# Revit family: 1195x595_START Panel Backlit UGR19
name_source: partatom
category: Lighting Fixtures
revit_build: Autodesk Revit 2017 (Build: 20190507_1515(x64)
units: mm (PartAtom-declared; Revit-internal decimal feet)

## family parameters
Cut with Voids When Loaded = No
Host = Face
Light Source = Yes
OmniClass Number = 23.80.70.00
OmniClass Title = Lighting
Part Type = Normal
Room Calculation Point = No
Round Connector Dimension = Use Diameter
Shared = No

## types (3) — shared parameters
-BOX_WIDTH_SYL = -40 mm
-LUMDEPTH_SYL = -277 mm
Apparent Load = 58 VA
Assembly Code = D5020200
AssetType = Fixed
BOX_WIDTH_SYL = 40 mm  [stored 0.131234 ft]
ClassificationName = Uniclass2015
ClassificationValue = EF_70_80
Color Filter = 16777215
DEPTH_SYL = 598 mm
Default Elevation = 1219 mm
Dimming Lamp Color Temperature Shift = <None>
DimmingControlOptions = http://www.sylvania-lighting.com
ElectricShockClassification = Class II
Emit Shape Visible in Rendering = No
Emit from Circle Diameter = 610 mm
HEIGHTBOTT_SYL = 7 mm  [stored 0.0229659 ft]
HEIGHT_SYL = 33 mm  [stored 0.108268 ft]
IfcExportAs = IfcLightFixtureType
IfcExportType = IfcLightFixtureType
ImpactProtectionIndex = IK03
IngressProtection = IP40/20
Keynote = 16500
LUMDEPTH_SYL = 277 mm
LUMWIDTH_SYL = 577 mm
Lamp = LED
LampColourRenderingIndex = 80
LampMacAdamStep = 6
LampsType = LED
LuminaireType = LED
MAINHEIGHT_SYL = 63 mm
Manufacturer = Feilo Sylvania
ManufacturerName = Feilo Sylvania
Material = aluminium,steel housing, other diffuser
Material_1_SYL = <By Category>
Material_2_SYL = <By Category>
Material_3_SYL = <By Category>
Material_4_SYL = <By Category>
NominalDepth = 595 mm  [stored 1.9521 ft]
NominalHeight = 35 mm
NominalLength = 1195 mm  [stored 3.9206 ft]
PowerConsumption = 58 W
PowerFactor = 0.9
TOP_DEPTH_SYL = 95 mm
TOP_WIDTH_SYL = 265 mm  [stored 0.869423 ft]
TOP__WIDTH_SYL = 545 mm
Tilt Angle = -90.00°
Type Image = <None>
URL = https://www.sylvania-lighting.com
Voltage = 0 V
WIDTH_SYL = 298 mm
Weight = 153.52 kg
zero-valued in all types: Cost

## per-type parameters (varying)
| type | DocumentationLiterature | LampColourTemperature | LampNominalLuminous | LuminousEfficacy | Model | ModelReference | Name | Photometric Web File |
| 0042203 | 102 | 6500 K | 5900 lm | 102 lm/W | START Panel UGR19 1200x600 5900Lm 865 LILO | START Panel UGR19 1200x600 5900Lm 865 LILO | START Panel UGR19 1200x600 5900Lm 865 LILO | 0042203.ies |
| 0042202 | 102 | 4000 K | 5900 lm | 102 lm/W | START Panel UGR19 1200x600 5900Lm 840 LILO | START Panel UGR19 1200x600 5900Lm 840 LILO | START Panel UGR19 1200x600 5900Lm 840 LILO | 0042202.ies |
| 0042201 | 98 | 3000 K | 5700 lm | 98 lm/W | START Panel UGR19 1200x600 5700Lm 830 LILO | START Panel UGR19 1200x600 5700Lm 830 LILO | START Panel UGR19 1200x600 5700Lm 830 LILO | 0042201.ies |

note: column(s) folded — value = type name in every type: ModelNumber, TypeName

note: [stored X ft] marks values corroborated as IEEE doubles in the binary element streams (Revit-internal decimal feet)

## geometry (parser evidence)
native form markers: Sweep x2
no freeform markers — native parametric forms only
